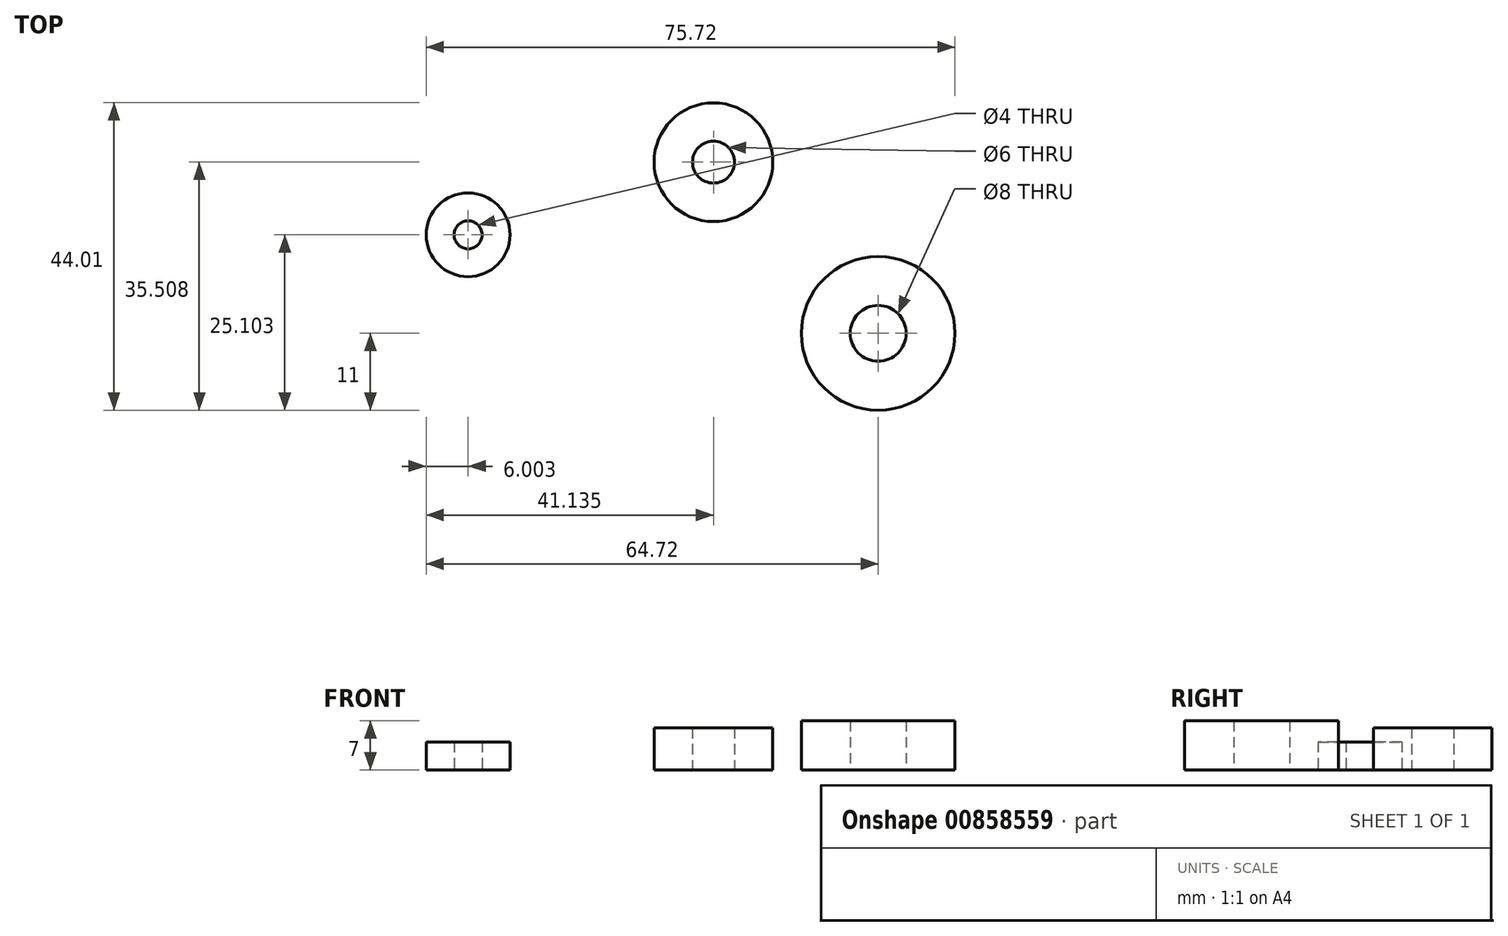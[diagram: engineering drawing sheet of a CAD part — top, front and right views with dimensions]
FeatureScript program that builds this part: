
annotation { "Feature Type Name" : "Feature", "Feature Type Description" : "" }
export const myFeature = defineFeature(function(context is Context, id is Id, definition is map)
    precondition{}
    {
        {
            var Q0;
            Q0=qCreatedBy(makeId("Top.planeOp"),FACE);
            var sketch = newSketch(context, id + "F0", { "sketchPlane" : qUnion([Q0])});
            skCircle(sketch, "E0", {"center": v(0, 0) * mm, "radius": 4 * mm});
            skCircle(sketch, "E1", {"center": v(0, 0) * mm, "radius": 11 * mm});
            skCircle(sketch, "E2", {"center": v(-58.72, 14.1) * mm, "radius": 2 * mm});
            skCircle(sketch, "E3", {"center": v(-58.72, 14.1) * mm, "radius": 6 * mm});
            skCircle(sketch, "E4", {"center": v(-23.59, 24.5) * mm, "radius": 3 * mm});
            skCircle(sketch, "E5", {"center": v(-23.59, 24.5) * mm, "radius": 8.5 * mm});
            skSolve(sketch);
        }
        {
            var Q0;
            Q0=makeQuery(id+"F0.imprint","IMPRINT",FACE,{"disambiguationData":[TD([[makeQuery(id+"F0.imprint","IMPRINT",EDGE,{"derivedFrom":sQuery(id+"F0.wireOp",EDGE,"E0")}),-1.0]])]});
            extrude(context, id + "F1", {"entities" : qUnion([Q0]), "depth" : 7 * mm, "offsetDistance" : 25.4 * mm});
        }
        {
            var Q0;
            Q0=makeQuery(id+"F0.imprint","IMPRINT",FACE,{"disambiguationData":[TD([[makeQuery(id+"F0.imprint","IMPRINT",EDGE,{"derivedFrom":sQuery(id+"F0.wireOp",EDGE,"E2")}),-1.0]])]});
            extrude(context, id + "F2", {"entities" : qUnion([Q0]), "depth" : 4 * mm, "offsetDistance" : 25.4 * mm});
        }
        {
            var Q0;
            Q0=makeQuery(id+"F0.imprint","IMPRINT",FACE,{"disambiguationData":[TD([[makeQuery(id+"F0.imprint","IMPRINT",EDGE,{"derivedFrom":sQuery(id+"F0.wireOp",EDGE,"E4")}),-1.0]])]});
            extrude(context, id + "F3", {"entities" : qUnion([Q0]), "depth" : 6 * mm, "offsetDistance" : 25.4 * mm});
        }
    });
